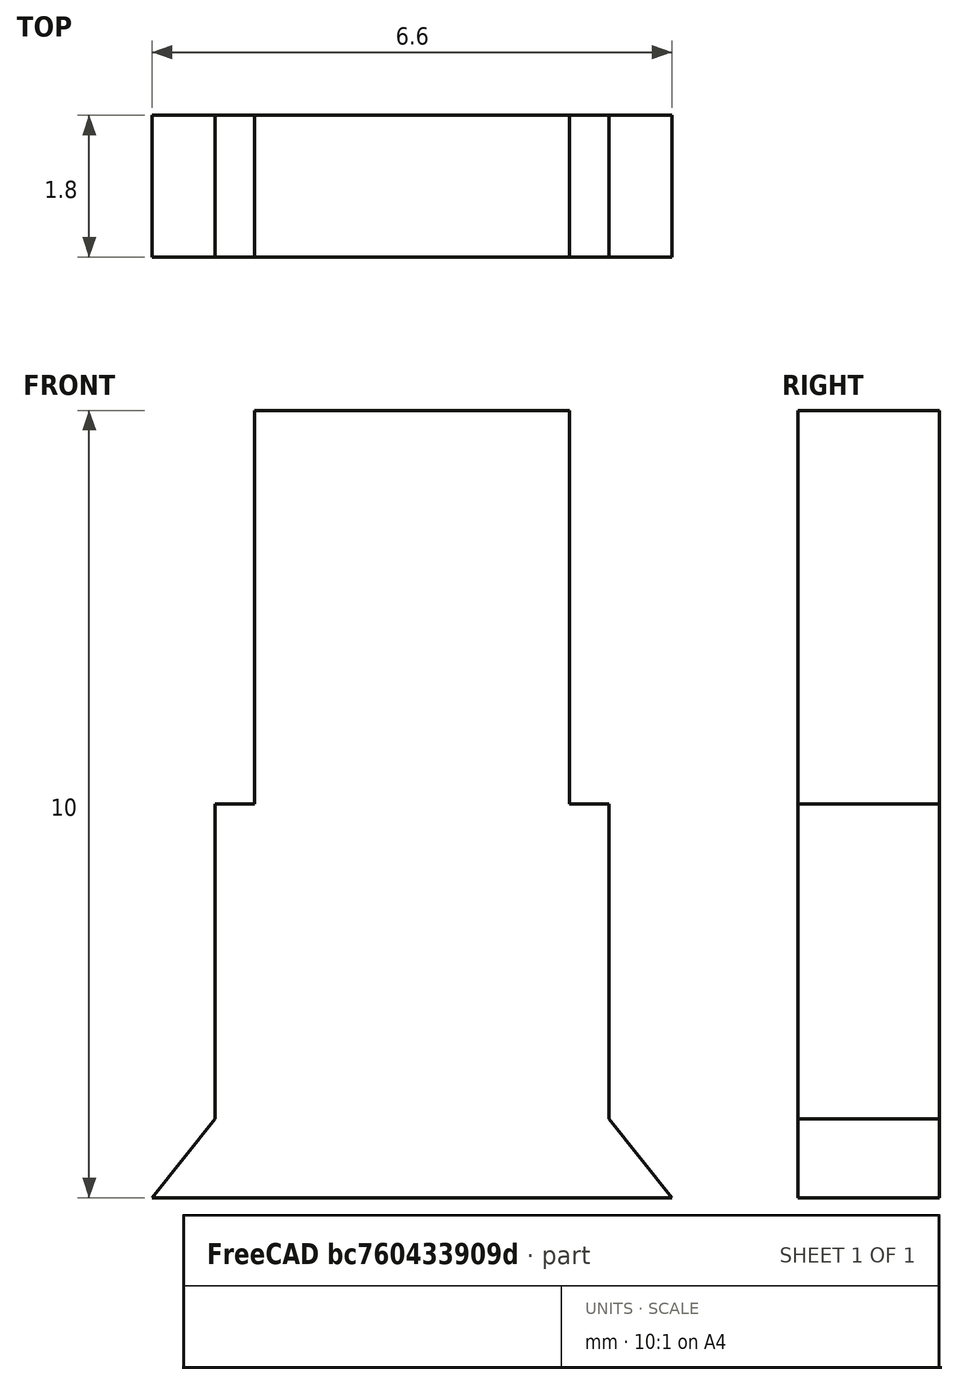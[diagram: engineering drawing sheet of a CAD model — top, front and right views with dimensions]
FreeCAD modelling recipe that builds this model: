
FCSTD DOCUMENT  (FreeCAD 0.14R2935 (Git))
Label: PTA1543-2010CI slide lever
License: CC-BY 3.0
LicenseURL: http://creativecommons.org/licenses/by/3.0/
objects: Sketcher::SketchObject×1, PartDesign::Pad×1
note: 3 computed .brp shape members not serialized (recipe doc carries the construction recipe); baked Part::Feature solids carry a one-line shape summary decoded from their .brp

FEATURE [Sketcher::SketchObject] Sketch
  Placement = pos=(0,0,0) rot=(-1,0,0;4.71239rad)
  sketch-geometry (10):
    g0: LineSegment StartX=-3.3 StartY=0 StartZ=0 EndX=3.3 EndY=0 EndZ=0
    g1: LineSegment StartX=3.3 StartY=0 StartZ=0 EndX=2.5 EndY=1 EndZ=0
    g2: LineSegment StartX=2.5 StartY=1 StartZ=0 EndX=2.5 EndY=5 EndZ=0
    g3: LineSegment StartX=2.5 StartY=5 StartZ=0 EndX=2 EndY=5 EndZ=0
    g4: LineSegment StartX=2 StartY=5 StartZ=0 EndX=2 EndY=10 EndZ=0
    g5: LineSegment StartX=2 StartY=10 StartZ=0 EndX=-2 EndY=10 EndZ=0
    g6: LineSegment StartX=-2 StartY=10 StartZ=0 EndX=-2 EndY=5 EndZ=0
    g7: LineSegment StartX=-2 StartY=5 StartZ=0 EndX=-2.5 EndY=5 EndZ=0
    g8: LineSegment StartX=-2.5 StartY=5 StartZ=0 EndX=-2.5 EndY=1 EndZ=0
    g9: LineSegment StartX=-2.5 StartY=1 StartZ=0 EndX=-3.3 EndY=0 EndZ=0
  constraints (29):
    c: PointOnObject(g0,g-1)
    c: Horizontal(g0)
    c: Coincident(g0,g1)
    c: Coincident(g1,g2)
    c: Vertical(g2)
    c: Coincident(g2,g3)
    c: Horizontal(g3)
    c: Coincident(g3,g4)
    c: Vertical(g4)
    c: Coincident(g4,g5)
    c: Horizontal(g5)
    c: Coincident(g5,g6)
    c: Vertical(g6)
    c: Coincident(g6,g7)
    c: Horizontal(g7)
    c: Coincident(g7,g8)
    c: Vertical(g8)
    c: Coincident(g8,g9)
    c: Coincident(g9,g0)
    c: Symmetric(g5,g4,g-2)
    c: Symmetric(g7,g2,g-2)
    c: Symmetric(g8,g1,g-2)
    c: Symmetric(g0,g0,g-2)
    c: DistanceX(g4,g5) = -4
    c: DistanceX(g7,g2) = 5
    c: DistanceY(g4,g3) = -5
    c: DistanceY(g4,g0) = -10
    c: DistanceX(g0,g0) = 6.6
    c: DistanceY(g1,g0) = -1
FEATURE [PartDesign::Pad] Pad
  Length = 1.8
  Length2 = 100
  Midplane = true
  Placement = pos=(0,0,0) rot=(-1,0,0;4.71239rad)
  Sketch = -> Sketch
  Type = 0
